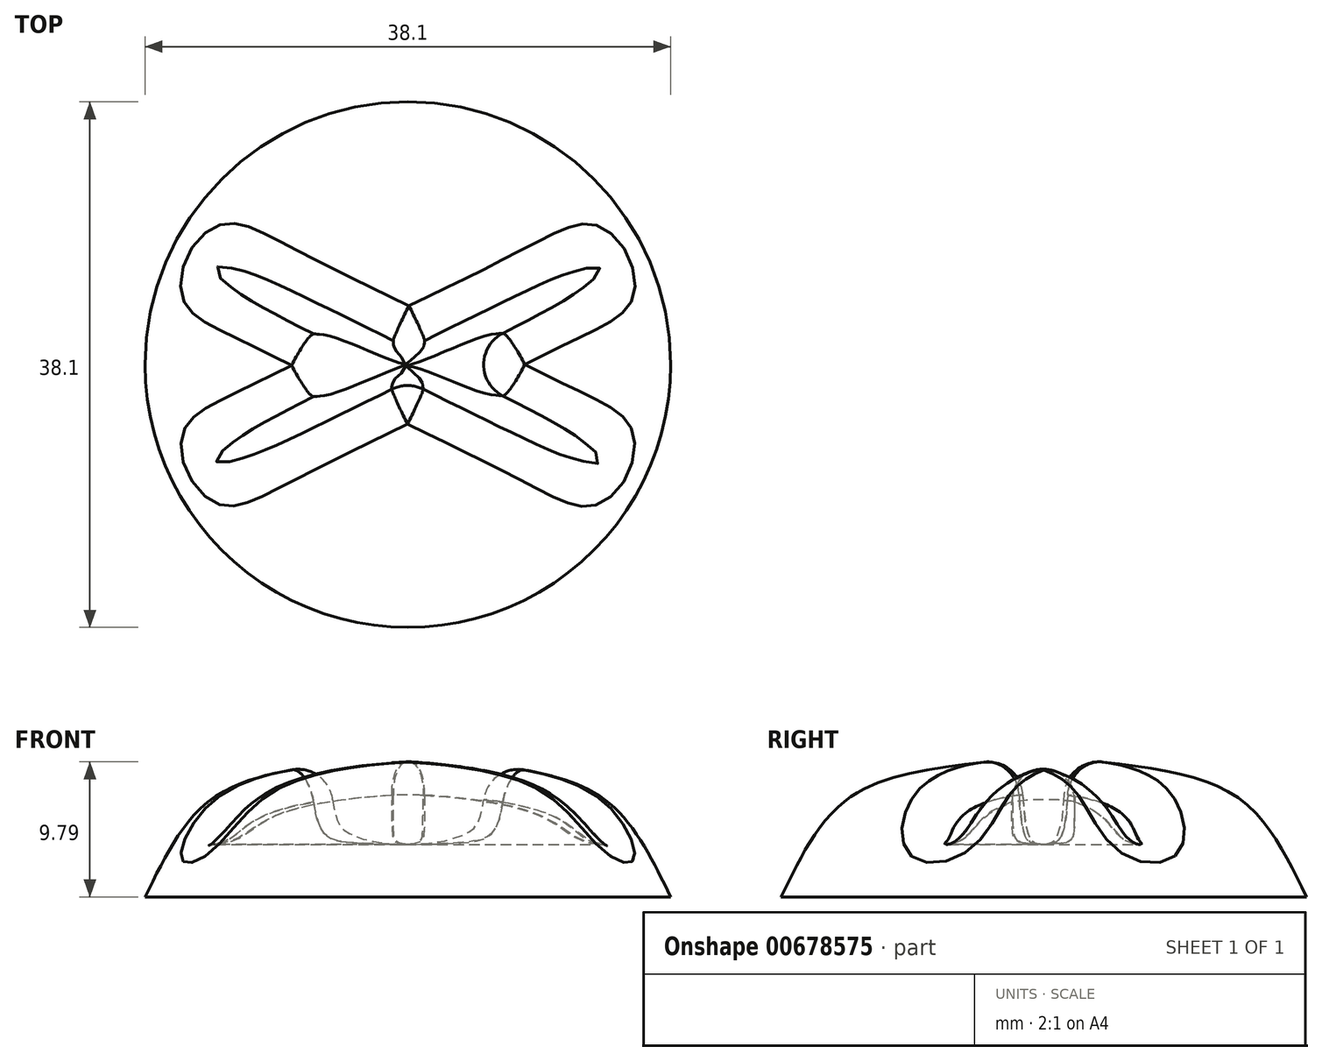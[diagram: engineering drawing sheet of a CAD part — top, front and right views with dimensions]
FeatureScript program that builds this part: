
annotation { "Feature Type Name" : "Feature", "Feature Type Description" : "" }
export const myFeature = defineFeature(function(context is Context, id is Id, definition is map)
    precondition{}
    {
        {
            var Q0;
            Q0=qCreatedBy(makeId("Front.planeOp"),FACE);
            var sketch = newSketch(context, id + "F0", { "sketchPlane" : qUnion([Q0])});
            skLineSegment(sketch, "E0", {"start": v(0, 0) * mm, "end": v(0, 10.16) * mm});
            skLineSegment(sketch, "E1", {"start": v(0, 0) * mm, "end": v(19.05, 0) * mm});
            skFitSpline(sketch, "E2", {"points": [v(0, 10.16) * mm, v(9.64, 8.96) * mm, v(15.08, 6.37) * mm, v(19.05, 0) * mm], "startDerivative": vector(27.4, -2.27) * mm, "endDerivative": vector(10.72, -21.91) * mm});
            skSolve(sketch);
        }
        {
            var Q0;
            Q0=makeQuery(id+"F0.imprint","IMPRINT",FACE,{"disambiguationData":[TD([[makeQuery(id+"F0.imprint","IMPRINT",EDGE,{"derivedFrom":sQuery(id+"F0.wireOp",EDGE,"E0")}),-1.0]])]});
            var Q1;
            Q1=sQuery(id+"F0.wireOp",EDGE,"E0");
            revolve(context, id + "F1", {"surfaceOperationType" : NewSurfaceOperationType.NEW, "entities" : qUnion([Q0]), "axis" : qUnion([Q1]), "revolveType" : RevolveType.FULL});
        }
        {
            var Q0;
            Q0=qCreatedBy(makeId("Top.planeOp"),FACE);
            cPlane(context, id + "F2", {"entities" : qUnion([Q0]), "cplaneType" : CPlaneType.OFFSET, "offset" : 6.1 * mm, "width" : 152.4 * mm, "height" : 152.4 * mm});
        }
        {
            var Q0;
            Q0=qCreatedBy(id+"F2.planeOp",FACE);
            var sketch = newSketch(context, id + "F3", { "sketchPlane" : qUnion([Q0])});
            skLineSegment(sketch, "E3", {"start": v(25.4, -12.7) * mm, "end": v(-25.4, 12.7) * mm});
            skLineSegment(sketch, "E4", {"start": v(25.4, 12.7) * mm, "end": v(-25.4, -12.7) * mm});
            skSolve(sketch);
        }
        {
            var Q0;
            Q0=qCreatedBy(makeId("Right.planeOp"),FACE);
            cPlane(context, id + "F4", {"entities" : qUnion([Q0]), "cplaneType" : CPlaneType.OFFSET, "offset" : 25.4 * mm, "width" : 152.4 * mm, "height" : 152.4 * mm});
        }
        {
            var Q0;
            Q0=qCreatedBy(id+"F4.planeOp",FACE);
            var sketch = newSketch(context, id + "F5", { "sketchPlane" : qUnion([Q0])});
            skLineSegment(sketch, "E5", {"start": v(-14, 11.23) * mm, "end": v(-11.47, 11.23) * mm});
            skLineSegment(sketch, "E6", {"start": v(13.91, 11.23) * mm, "end": v(11.37, 11.23) * mm});
            skFitSpline(sketch, "E7", {"points": [v(-14, 11.23) * mm, v(-12.74, 3.81) * mm, v(-11.47, 11.23) * mm], "startDerivative": vector(0, -44.74) * mm, "endDerivative": vector(-0.73, 44.25) * mm});
            skFitSpline(sketch, "E8", {"points": [v(11.37, 11.23) * mm, v(12.64, 3.81) * mm, v(13.91, 11.23) * mm], "startDerivative": vector(0.6, -44.85) * mm, "endDerivative": vector(0, 45.24) * mm});
            skPoint(sketch, "E9.start.orphan", {"position": v(-12.74, 11.23) * mm});
            skPoint(sketch, "E10.start.orphan", {"position": v(12.64, 11.23) * mm});
            skSolve(sketch);
        }
        {
            var Q0;
            Q0=makeQuery(id+"F5.imprint","IMPRINT",FACE,{"disambiguationData":[TD([[makeQuery(id+"F5.imprint","IMPRINT",EDGE,{"derivedFrom":sQuery(id+"F5.wireOp",EDGE,"E5")}),-1.0]])]});
            var Q1;
            Q1=sQuery(id+"F3.wireOp",EDGE,"E3");
            sweep(context, id + "F6", {"operationType" : NewBodyOperationType.REMOVE, "profiles" : qUnion([Q0]), "path" : qUnion([Q1])});
        }
        {
            var Q0;
            Q0=makeQuery(id+"F5.imprint","IMPRINT",FACE,{"disambiguationData":[TD([[makeQuery(id+"F5.imprint","IMPRINT",EDGE,{"derivedFrom":sQuery(id+"F5.wireOp",EDGE,"E6")}),1.0]])]});
            var Q1;
            Q1=sQuery(id+"F3.wireOp",EDGE,"E4");
            sweep(context, id + "F7", {"operationType" : NewBodyOperationType.REMOVE, "profiles" : qUnion([Q0]), "path" : qUnion([Q1])});
        }
        {
            var Q0;
            Q0=makeQuery(id+"F7.boolean.opBoolean","INTERSECT",EDGE,{"disambiguationData":[OD(0.0)],"derivedFrom":[makeQuery(id+"F1.opRevolve","SWEPT_FACE",FACE,{"disambiguationData":[OSD([sQuery(id+"F0.wireOp",EDGE,"E2")])]}),makeQuery(id+"F7.opSweep","SWEPT_FACE",FACE,{"disambiguationData":[OSD([sQuery(id+"F3.wireOp",EDGE,"E4"),sQuery(id+"F5.wireOp",EDGE,"E8")])]})]});
            var Q1;
            Q1=makeQuery(id+"F7.boolean.opBoolean","SPLIT",EDGE,{"disambiguationData":[OD(1.0)],"derivedFrom":makeQuery(id+"F6.boolean.opBoolean","INTERSECT",EDGE,{"derivedFrom":[makeQuery(id+"F1.opRevolve","SWEPT_FACE",FACE,{"disambiguationData":[OSD([sQuery(id+"F0.wireOp",EDGE,"E2")])]}),makeQuery(id+"F6.opSweep","SWEPT_FACE",FACE,{"disambiguationData":[OSD([sQuery(id+"F3.wireOp",EDGE,"E3"),sQuery(id+"F5.wireOp",EDGE,"E7")])]})]})});
            var Q2;
            Q2=makeQuery(id+"F7.boolean.opBoolean","INTERSECT",EDGE,{"disambiguationData":[OD(1.0)],"derivedFrom":[makeQuery(id+"F1.opRevolve","SWEPT_FACE",FACE,{"disambiguationData":[OSD([sQuery(id+"F0.wireOp",EDGE,"E2")])]}),makeQuery(id+"F7.opSweep","SWEPT_FACE",FACE,{"disambiguationData":[OSD([sQuery(id+"F3.wireOp",EDGE,"E4"),sQuery(id+"F5.wireOp",EDGE,"E8")])]})]});
            var Q3;
            Q3=makeQuery(id+"F7.boolean.opBoolean","SPLIT",EDGE,{"disambiguationData":[OD(0.0)],"derivedFrom":makeQuery(id+"F6.boolean.opBoolean","INTERSECT",EDGE,{"derivedFrom":[makeQuery(id+"F1.opRevolve","SWEPT_FACE",FACE,{"disambiguationData":[OSD([sQuery(id+"F0.wireOp",EDGE,"E2")])]}),makeQuery(id+"F6.opSweep","SWEPT_FACE",FACE,{"disambiguationData":[OSD([sQuery(id+"F3.wireOp",EDGE,"E3"),sQuery(id+"F5.wireOp",EDGE,"E7")])]})]})});
            var Q4;
            Q4=makeQuery(id+"F7.boolean.opBoolean","INTERSECT",EDGE,{"disambiguationData":[OD(1.0)],"derivedFrom":[makeQuery(id+"F6.boolean.opBoolean","COPY",FACE,{"derivedFrom":makeQuery(id+"F6.opSweep","SWEPT_FACE",FACE,{"disambiguationData":[OSD([sQuery(id+"F3.wireOp",EDGE,"E3"),sQuery(id+"F5.wireOp",EDGE,"E7")])]})}),makeQuery(id+"F7.opSweep","SWEPT_FACE",FACE,{"disambiguationData":[OSD([sQuery(id+"F3.wireOp",EDGE,"E4"),sQuery(id+"F5.wireOp",EDGE,"E8")])]})]});
            var Q5;
            Q5=makeQuery(id+"F7.boolean.opBoolean","INTERSECT",EDGE,{"disambiguationData":[OD(0.0)],"derivedFrom":[makeQuery(id+"F6.boolean.opBoolean","COPY",FACE,{"derivedFrom":makeQuery(id+"F6.opSweep","SWEPT_FACE",FACE,{"disambiguationData":[OSD([sQuery(id+"F3.wireOp",EDGE,"E3"),sQuery(id+"F5.wireOp",EDGE,"E7")])]})}),makeQuery(id+"F7.opSweep","SWEPT_FACE",FACE,{"disambiguationData":[OSD([sQuery(id+"F3.wireOp",EDGE,"E4"),sQuery(id+"F5.wireOp",EDGE,"E8")])]})]});
            fillet(context, id + "F8", {"entities" : qUnion([Q0, Q1, Q2, Q3, Q4, Q5]), "radius" : 2.54 * mm, "tangentPropagation" : true, "allowEdgeOverflow" : false});
        }
    });
